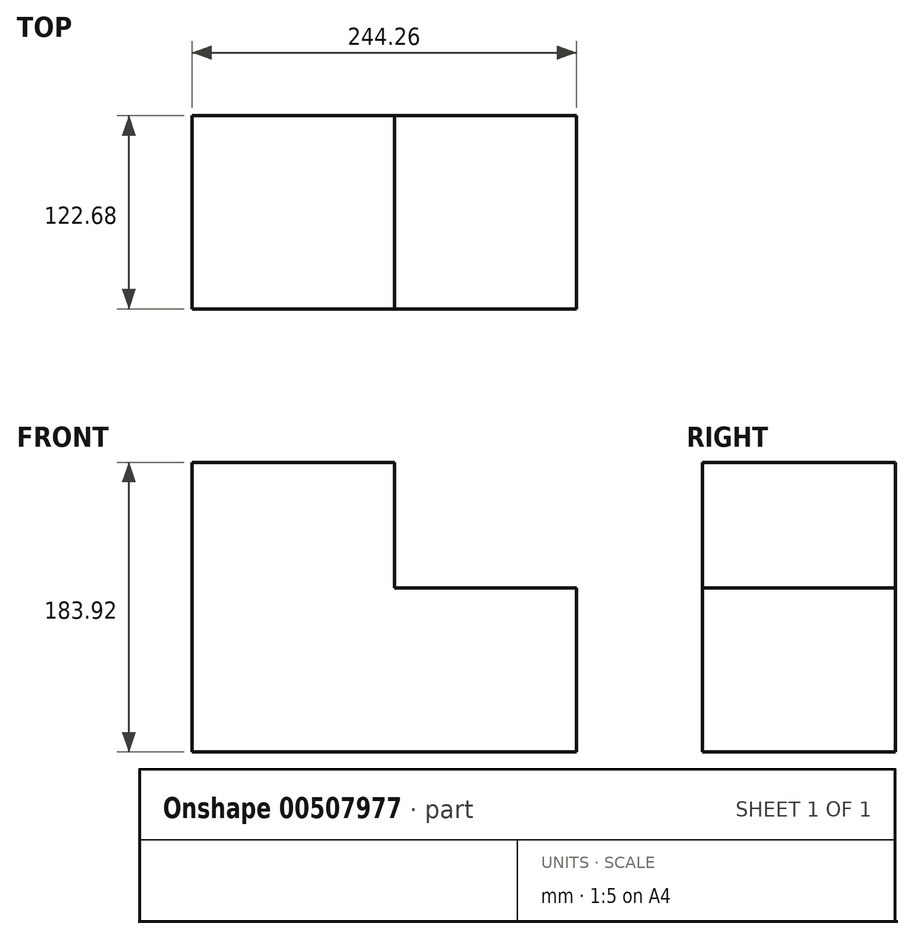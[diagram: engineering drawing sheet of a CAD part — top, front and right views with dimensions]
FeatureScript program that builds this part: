
annotation { "Feature Type Name" : "Feature", "Feature Type Description" : "" }
export const myFeature = defineFeature(function(context is Context, id is Id, definition is map)
    precondition{}
    {
        {
            var Q0;
            Q0=qCreatedBy(makeId("Front.planeOp"),FACE);
            var sketch = newSketch(context, id + "F0", { "sketchPlane" : qUnion([Q0])});
            skLineSegment(sketch, "E0", {"start": v(0, 81.88) * mm, "end": v(0, 1.98) * mm});
            skLineSegment(sketch, "E1", {"start": v(0, 1.98) * mm, "end": v(115.53, 1.98) * mm});
            skLineSegment(sketch, "E2", {"start": v(-128.73, 81.88) * mm, "end": v(-128.73, -102.04) * mm});
            skLineSegment(sketch, "E3", {"start": v(-128.73, -102.04) * mm, "end": v(115.53, -102.04) * mm});
            skLineSegment(sketch, "E4", {"start": v(115.53, -102.04) * mm, "end": v(115.53, 1.98) * mm});
            skLineSegment(sketch, "E5", {"start": v(-128.73, 81.88) * mm, "end": v(0, 81.88) * mm});
            skSolve(sketch);
        }
        {
            var Q0;
            Q0=makeQuery(id+"F0.imprint","IMPRINT",FACE,{"disambiguationData":[TD([[makeQuery(id+"F0.imprint","IMPRINT",EDGE,{"derivedFrom":sQuery(id+"F0.wireOp",EDGE,"E0")}),-1.0]])]});
            extrude(context, id + "F1", {"entities" : qUnion([Q0]), "depth" : 122.68 * mm});
        }
    });
